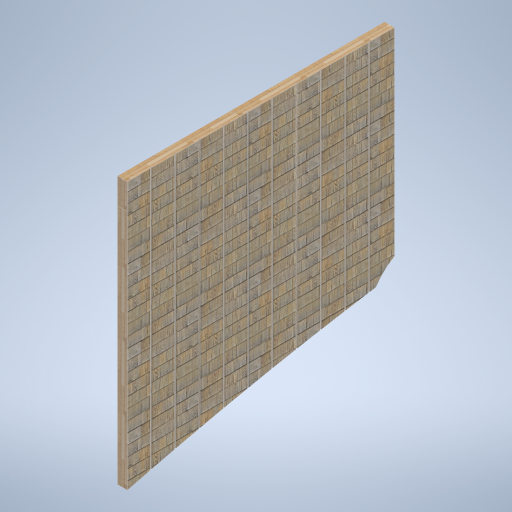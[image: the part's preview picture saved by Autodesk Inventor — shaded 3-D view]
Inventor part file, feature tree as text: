
AUTODESK INVENTOR PART (.ipt)
format: ipt  version: 2024.2 (Build 282272000, 272)  size: 506,368 bytes
history: native  units: in
note: dims shown in document units (in); Inventor stores cm internally (conversion verified against a paired STEP export)
features: other x3, sketch x2
ambient origin geometry x8: Origin, YZ Plane, XZ Plane, XY Plane, X Axis, Y Axis, Z Axis, Center Point
bodies: Solid1 (feature_tree)
feature tree (5):
  other  "side_wall_01.ipt"
  other  "Solid1::side_wall_01.ipt"
  other  "TaggingFeature1"
  sketch  "Sketch1"  dims[d0=0.3937in]
  sketch  "Sketch2"
